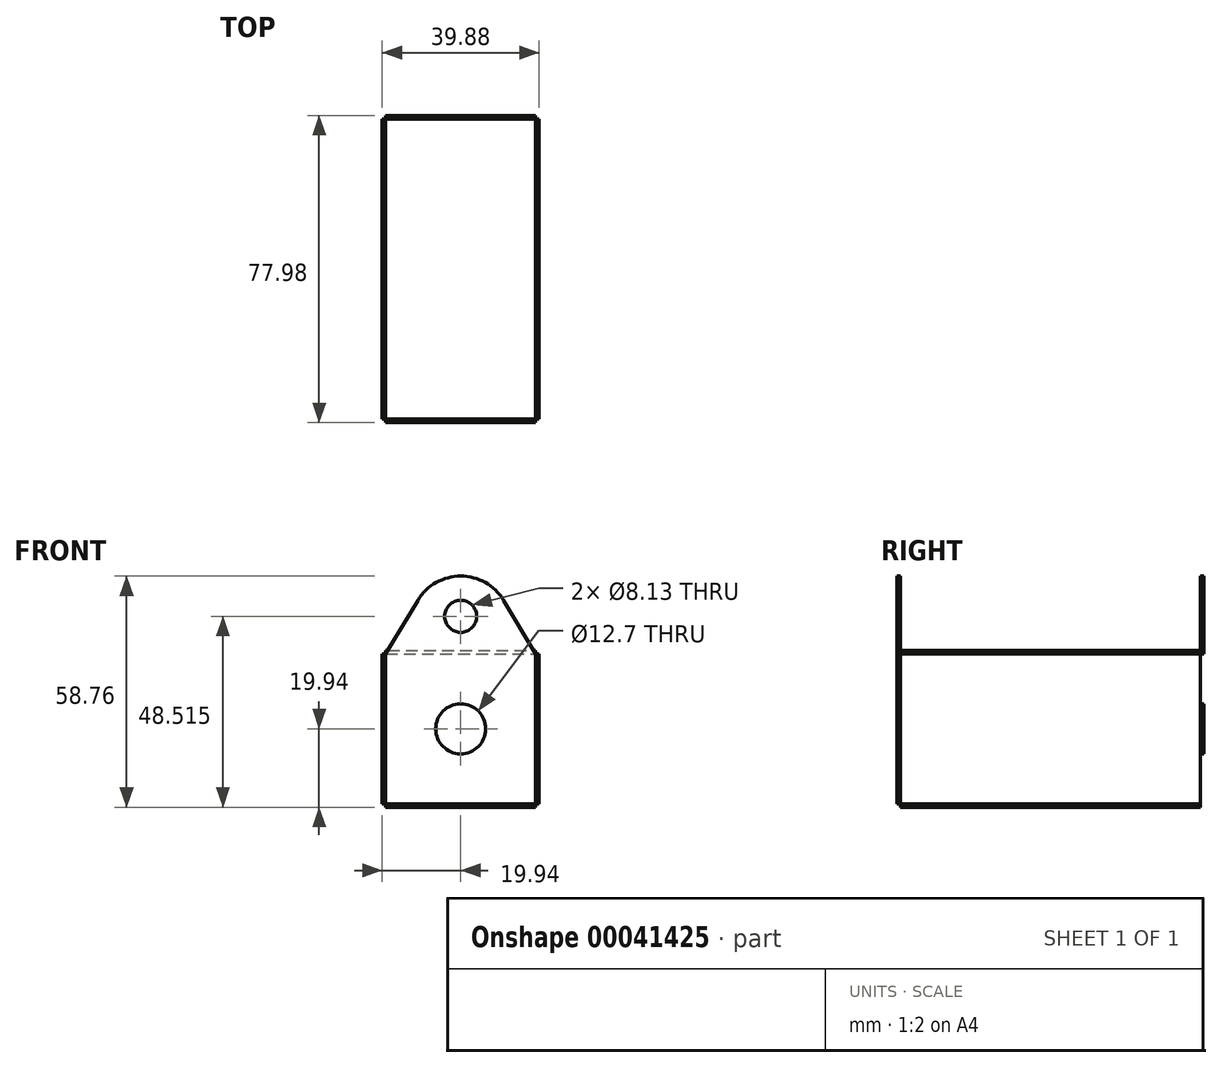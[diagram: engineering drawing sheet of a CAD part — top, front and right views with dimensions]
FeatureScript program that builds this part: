
annotation { "Feature Type Name" : "Feature", "Feature Type Description" : "" }
export const myFeature = defineFeature(function(context is Context, id is Id, definition is map)
    precondition{}
    {
        {
            var Q0;
            Q0=qCreatedBy(makeId("Front.planeOp"),FACE);
            var sketch = newSketch(context, id + "F0", { "sketchPlane" : qUnion([Q0])});
            skLineSegment(sketch, "E0.bottom", {"start": v(0, 0) * mm, "end": v(38.1, 0) * mm});
            skLineSegment(sketch, "E0.top", {"start": v(0, 38.1) * mm, "end": v(38.1, 38.1) * mm});
            skLineSegment(sketch, "E0.left", {"start": v(0, 0) * mm, "end": v(0, 38.1) * mm});
            skLineSegment(sketch, "E0.right", {"start": v(38.1, 0) * mm, "end": v(38.1, 38.1) * mm});
            skLineSegment(sketch, "E1.0", {"start": v(0, -0.89) * mm, "end": v(38.1, -0.89) * mm});
            skLineSegment(sketch, "E1.1", {"start": v(-0.89, 0) * mm, "end": v(-0.89, 38.1) * mm});
            skLineSegment(sketch, "E1.2", {"start": v(0, 38.99) * mm, "end": v(38.1, 38.99) * mm});
            skLineSegment(sketch, "E1.3", {"start": v(38.99, 0) * mm, "end": v(38.99, 38.1) * mm});
            skLineSegment(sketch, "E2", {"start": v(0, 0) * mm, "end": v(-0.89, 0) * mm});
            skLineSegment(sketch, "E3", {"start": v(0, 0) * mm, "end": v(0, -0.89) * mm});
            skLineSegment(sketch, "E4", {"start": v(0, 38.1) * mm, "end": v(0, 38.99) * mm});
            skLineSegment(sketch, "E5", {"start": v(0, 38.1) * mm, "end": v(-0.89, 38.1) * mm});
            skLineSegment(sketch, "E6", {"start": v(38.1, 38.1) * mm, "end": v(38.99, 38.1) * mm});
            skLineSegment(sketch, "E7", {"start": v(38.1, 38.1) * mm, "end": v(38.1, 38.99) * mm});
            skLineSegment(sketch, "E8", {"start": v(38.1, 0) * mm, "end": v(38.1, -0.89) * mm});
            skLineSegment(sketch, "E9", {"start": v(38.1, 0) * mm, "end": v(38.99, 0) * mm});
            skSolve(sketch);
        }
        {
            var Q0;
            Q0=makeQuery(id+"F0.imprint","IMPRINT",FACE,{"disambiguationData":[TD([[makeQuery(id+"F0.imprint","IMPRINT",EDGE,{"derivedFrom":sQuery(id+"F0.wireOp",EDGE,"E0.bottom")}),-1.0]])]});
            var Q1;
            Q1=makeQuery(id+"F0.imprint","IMPRINT",FACE,{"disambiguationData":[TD([[makeQuery(id+"F0.imprint","IMPRINT",EDGE,{"derivedFrom":sQuery(id+"F0.wireOp",EDGE,"E0.left")}),1.0]])]});
            var Q2;
            Q2=makeQuery(id+"F0.imprint","IMPRINT",FACE,{"disambiguationData":[TD([[makeQuery(id+"F0.imprint","IMPRINT",EDGE,{"derivedFrom":sQuery(id+"F0.wireOp",EDGE,"E0.top")}),1.0]])]});
            var Q3;
            Q3=makeQuery(id+"F0.imprint","IMPRINT",FACE,{"disambiguationData":[TD([[makeQuery(id+"F0.imprint","IMPRINT",EDGE,{"derivedFrom":sQuery(id+"F0.wireOp",EDGE,"E0.right")}),-1.0]])]});
            extrude(context, id + "F1", {"entities" : qUnion([Q0, Q1, Q2, Q3]), "depth" : 76.2 * mm});
        }
        {
            var Q0;
            Q0=makeQuery(id+"F1.opExtrude","CAP_FACE",FACE,{"disambiguationData":[OSD([sQuery(id+"F0.wireOp",EDGE,"E0.top"),sQuery(id+"F0.wireOp",EDGE,"E1.2"),sQuery(id+"F0.wireOp",EDGE,"E4"),sQuery(id+"F0.wireOp",EDGE,"E7")])],"isStart":false});
            var sketch = newSketch(context, id + "F2", { "sketchPlane" : qUnion([Q0])});
            skLineSegment(sketch, "E10.top", {"start": v(0, 0) * mm, "end": v(38.1, 0) * mm});
            skLineSegment(sketch, "E10.left", {"start": v(0, 38.1) * mm, "end": v(0, 0) * mm});
            skLineSegment(sketch, "E10.right", {"start": v(38.1, 38.1) * mm, "end": v(38.1, 0) * mm});
            skLineSegment(sketch, "E11", {"start": v(0, 38.1) * mm, "end": v(38.1, 0) * mm, "construction": true});
            skLineSegment(sketch, "E12", {"start": v(38.1, 38.1) * mm, "end": v(0, 0) * mm, "construction": true});
            skCircle(sketch, "E13", {"center": v(19.05, 19.05) * mm, "radius": 6.35 * mm});
            skLineSegment(sketch, "E14", {"start": v(0, 38.1) * mm, "end": v(8.16, 51.7) * mm});
            skLineSegment(sketch, "E15", {"start": v(29.94, 51.7) * mm, "end": v(38.1, 38.1) * mm});
            skLineSegment(sketch, "E16", {"start": v(19.05, 0) * mm, "end": v(19.05, 72.15) * mm, "construction": true});
            skPoint(sketch, "E17.visualSharp", {"position": v(19.05, 69.85) * mm});
            skArc(sketch, "E17.filletArc", {"start": v(29.94, 51.7) * mm, "mid": v(19.05, 57.87) * mm, "end": v(8.16, 51.7) * mm});
            skCircle(sketch, "E18", {"center": v(19.05, 47.62) * mm, "radius": 4.06 * mm});
            skSolve(sketch);
        }
        {
            var Q0;
            {var subQ5=sQuery(id+"F2.wireOp",EDGE,"E17.filletArc");Q0=makeQuery(id+"F2.imprint","IMPRINT",FACE,{"disambiguationData":[TD([[makeQuery(id+"F2.imprint","IMPRINT",EDGE,{"derivedFrom":subQ5}),1.0]])]});}
            var Q1;
            Q1=makeQuery(id+"F2.imprint","IMPRINT",FACE,{"disambiguationData":[TD([[makeQuery(id+"F2.imprint","IMPRINT",EDGE,{"derivedFrom":sQuery(id+"F2.wireOp",EDGE,"E10.top")}),1.0]])]});
            var Q2;
            {var subQ0=makeQuery(id+"F1.opExtrude","CAP_EDGE",EDGE,{"disambiguationData":[OSD([sQuery(id+"F0.wireOp",EDGE,"E0.top")])],"isStart":false});Q2=makeQuery(id+"F2.imprint","IMPRINT",FACE,{"disambiguationData":[TD([[makeQuery(id+"F2.imprint","IMPRINT",EDGE,{"derivedFrom":subQ0}),1.0]])]});}
            extrude(context, id + "F3", {"entities" : qUnion([Q0, Q1, Q2]), "operationType" : NewBodyOperationType.ADD, "depth" : 0.89 * mm});
        }
        {
            var Q0;
            Q0=makeQuery(id+"F1.opExtrude","CAP_FACE",FACE,{"disambiguationData":[OSD([sQuery(id+"F0.wireOp",EDGE,"E0.top"),sQuery(id+"F0.wireOp",EDGE,"E1.2"),sQuery(id+"F0.wireOp",EDGE,"E4"),sQuery(id+"F0.wireOp",EDGE,"E7")])],"isStart":true});
            var sketch = newSketch(context, id + "F4", { "sketchPlane" : qUnion([Q0])});
            skPoint(sketch, "E19.0", {"position": v(-19.05, 45.17) * mm});
            skLineSegment(sketch, "E20.0.0", {"start": v(-8.16, 51.7) * mm, "end": v(-0.53, 38.99) * mm});
            skLineSegment(sketch, "E20.0.1", {"start": v(-0.53, 38.99) * mm, "end": v(-37.57, 38.99) * mm});
            skLineSegment(sketch, "E20.0.2", {"start": v(-37.57, 38.99) * mm, "end": v(-29.94, 51.7) * mm});
            skArc(sketch, "E20.0.3", {"start": v(-29.94, 51.7) * mm, "mid": v(-19.05, 57.87) * mm, "end": v(-8.16, 51.7) * mm});
            skLineSegment(sketch, "E21.0.0", {"start": v(0.89, 38.1) * mm, "end": v(0.89, 0) * mm});
            skLineSegment(sketch, "E21.0.2", {"start": v(0.89, 0) * mm, "end": v(0.89, 38.1) * mm});
            skLineSegment(sketch, "E22.0.0", {"start": v(0, 38.1) * mm, "end": v(0, 0) * mm});
            skLineSegment(sketch, "E22.0.1", {"start": v(0, 0) * mm, "end": v(-38.1, 0) * mm});
            skLineSegment(sketch, "E22.0.2", {"start": v(-38.1, 0) * mm, "end": v(-38.1, 38.1) * mm});
            skLineSegment(sketch, "E22.0.3", {"start": v(-38.1, 38.1) * mm, "end": v(0, 38.1) * mm});
            skCircle(sketch, "E23.0", {"center": v(-19.05, 19.05) * mm, "radius": 6.35 * mm});
            skLineSegment(sketch, "E24.0", {"start": v(0, 38.99) * mm, "end": v(-0.53, 38.99) * mm});
            skLineSegment(sketch, "E25.2.0", {"start": v(-0.53, 38.99) * mm, "end": v(0, 38.1) * mm});
            skLineSegment(sketch, "E25.2.1", {"start": v(0, 38.1) * mm, "end": v(-38.1, 38.1) * mm});
            skLineSegment(sketch, "E25.2.2", {"start": v(-38.1, 38.1) * mm, "end": v(-37.57, 38.99) * mm});
            skLineSegment(sketch, "E25.2.3", {"start": v(-37.57, 38.99) * mm, "end": v(-0.53, 38.99) * mm});
            skCircle(sketch, "E26.0", {"center": v(-19.05, 47.62) * mm, "radius": 4.06 * mm});
            skSolve(sketch);
        }
        {
            var Q0;
            Q0=makeQuery(id+"F4.imprint","IMPRINT",FACE,{"disambiguationData":[TD([[makeQuery(id+"F4.imprint","IMPRINT",EDGE,{"derivedFrom":sQuery(id+"F4.wireOp",EDGE,"E20.0.0")}),-1.0]])]});
            var Q1;
            Q1=makeQuery(id+"F4.imprint","IMPRINT",FACE,{"disambiguationData":[TD([[makeQuery(id+"F4.imprint","IMPRINT",EDGE,{"derivedFrom":sQuery(id+"F4.wireOp",EDGE,"E25.2.0")}),-1.0]])]});
            var Q2;
            Q2=makeQuery(id+"F4.imprint","IMPRINT",FACE,{"disambiguationData":[TD([[makeQuery(id+"F4.imprint","IMPRINT",EDGE,{"derivedFrom":sQuery(id+"F4.wireOp",EDGE,"E23.0")}),1.0]])]});
            extrude(context, id + "F5", {"entities" : qUnion([Q0, Q1, Q2]), "operationType" : NewBodyOperationType.ADD, "depth" : 0.89 * mm});
        }
    });
